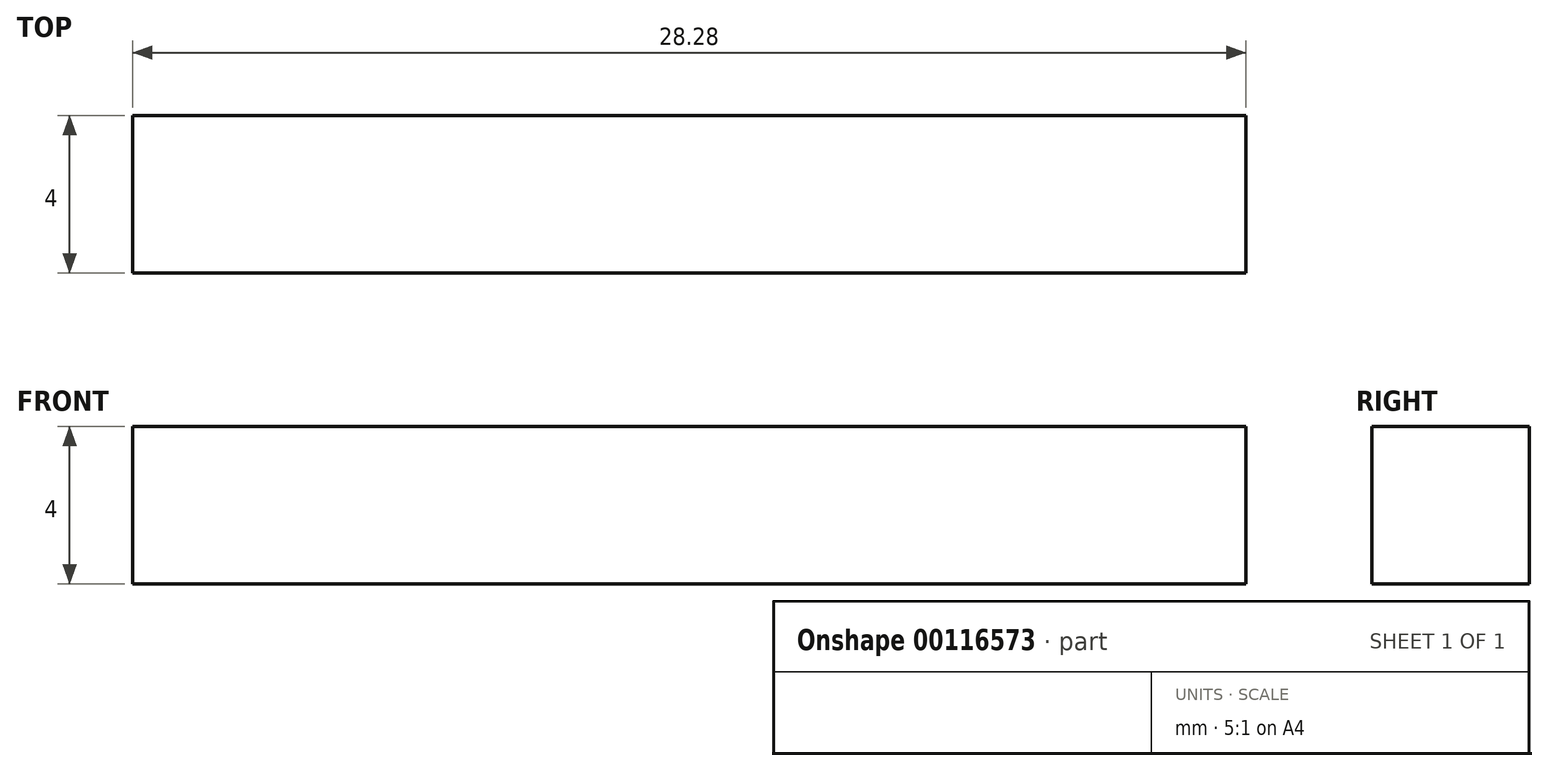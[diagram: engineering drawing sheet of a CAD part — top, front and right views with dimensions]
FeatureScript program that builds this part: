
annotation { "Feature Type Name" : "Feature", "Feature Type Description" : "" }
export const myFeature = defineFeature(function(context is Context, id is Id, definition is map)
    precondition{}
    {
        {
            var Q0;
            Q0=qCreatedBy(makeId("Top.planeOp"),FACE);
            var sketch = newSketch(context, id + "F0", { "sketchPlane" : qUnion([Q0])});
            skLineSegment(sketch, "E0.bottom", {"start": v(14.14, 2) * mm, "end": v(-14.14, 2) * mm});
            skLineSegment(sketch, "E0.top", {"start": v(14.14, -2) * mm, "end": v(-14.14, -2) * mm});
            skLineSegment(sketch, "E0.left", {"start": v(14.14, 2) * mm, "end": v(14.14, -2) * mm});
            skLineSegment(sketch, "E0.right", {"start": v(-14.14, 2) * mm, "end": v(-14.14, -2) * mm});
            skPoint(sketch, "E0.middle", {"position": v(0, 0) * mm});
            skSolve(sketch);
        }
        {
            var Q0;
            Q0=makeQuery(id+"F0.imprint","IMPRINT",FACE,{"disambiguationData":[TD([[makeQuery(id+"F0.imprint","IMPRINT",EDGE,{"derivedFrom":sQuery(id+"F0.wireOp",EDGE,"E0.bottom")}),1.0]])]});
            extrude(context, id + "F1", {"entities" : qUnion([Q0]), "depth" : 4 * mm});
        }
    });
